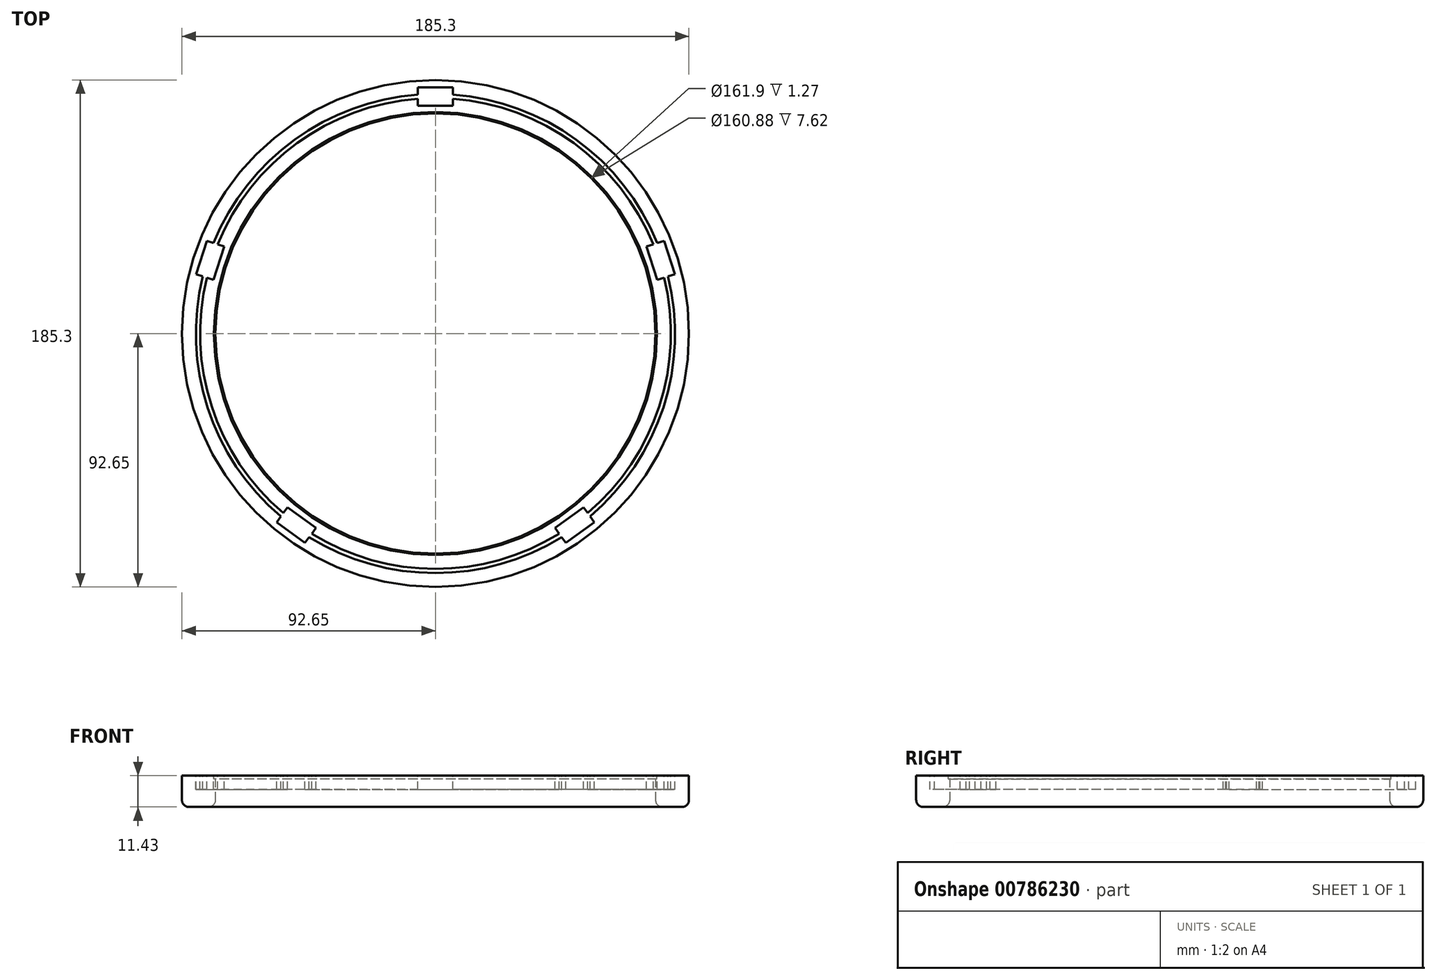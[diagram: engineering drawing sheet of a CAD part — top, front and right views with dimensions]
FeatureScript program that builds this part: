
annotation { "Feature Type Name" : "Feature", "Feature Type Description" : "" }
export const myFeature = defineFeature(function(context is Context, id is Id, definition is map)
    precondition{}
    {
        {
            var Q0;
            Q0=qCreatedBy(makeId("Front.planeOp"),FACE);
            var sketch = newSketch(context, id + "F0", { "sketchPlane" : qUnion([Q0])});
            skLineSegment(sketch, "E0", {"start": v(0, 91.39) * mm, "end": v(0, -94.44) * mm, "construction": true});
            skLineSegment(sketch, "E1", {"start": v(5.08, 0) * mm, "end": v(5.08, -10.16) * mm});
            skLineSegment(sketch, "E2", {"start": v(5.08, -10.16) * mm, "end": v(92.65, -10.16) * mm});
            skLineSegment(sketch, "E3", {"start": v(5.08, 0) * mm, "end": v(80.95, 0) * mm});
            skLineSegment(sketch, "E4.top", {"start": v(86.03, 1.27) * mm, "end": v(80.95, 1.27) * mm});
            skLineSegment(sketch, "E4.left", {"start": v(86.03, -3.8) * mm, "end": v(86.03, 1.27) * mm});
            skLineSegment(sketch, "E4.right", {"start": v(80.95, 0) * mm, "end": v(80.95, 1.27) * mm});
            skLineSegment(sketch, "E5.top", {"start": v(87.57, 1.27) * mm, "end": v(92.65, 1.27) * mm});
            skLineSegment(sketch, "E5.left", {"start": v(87.57, -3.8) * mm, "end": v(87.57, 1.27) * mm});
            skLineSegment(sketch, "E5.right", {"start": v(92.65, -10.16) * mm, "end": v(92.65, 1.27) * mm});
            skLineSegment(sketch, "E6", {"start": v(86.03, -3.8) * mm, "end": v(87.57, -3.8) * mm});
            skSolve(sketch);
        }
        {
            var Q0;
            Q0=qSketchRegion(id+"F0",true);
            var Q1;
            Q1=sQuery(id+"F0.wireOp",EDGE,"E0");
            revolve(context, id + "F1", {"surfaceOperationType" : NewSurfaceOperationType.NEW, "entities" : qUnion([Q0]), "axis" : qUnion([Q1]), "revolveType" : RevolveType.FULL});
        }
        {
            var Q0;
            Q0=makeQuery(id+"F1.opRevolve","SWEPT_FACE",FACE,{"disambiguationData":[OSD([sQuery(id+"F0.wireOp",EDGE,"E2")])]});
            var sketch = newSketch(context, id + "F2", { "sketchPlane" : qUnion([Q0])});
            skArc(sketch, "E7", {"start": v(-3.18, 80.38) * mm, "mid": v(-56.88, 56.88) * mm, "end": v(-80.38, 3.18) * mm});
            skLineSegment(sketch, "E8", {"start": v(0, 14.6) * mm, "end": v(0, 80.44) * mm, "construction": true});
            skLineSegment(sketch, "E9", {"start": v(14.6, 0) * mm, "end": v(80.44, 0) * mm, "construction": true});
            skLineSegment(sketch, "E10", {"start": v(0, -14.6) * mm, "end": v(0, -80.44) * mm, "construction": true});
            skLineSegment(sketch, "E11", {"start": v(-14.6, 0) * mm, "end": v(-80.44, 0) * mm, "construction": true});
            skArc(sketch, "E12.trimOffspring", {"start": v(-80.38, 3.18) * mm, "mid": v(-58, -55.75) * mm, "end": v(0, -80.44) * mm});
            skArc(sketch, "E13.trimOffspring", {"start": v(80.38, -3.17) * mm, "mid": v(56.88, 56.88) * mm, "end": v(-3.18, 80.38) * mm});
            skArc(sketch, "E14.trimOffspring", {"start": v(-3.17, -80.38) * mm, "mid": v(54.6, -59.08) * mm, "end": v(80.38, -3.17) * mm});
            skSolve(sketch);
        }
        {
            var Q0;
            Q0 = qSketchRegion(id + "F2", true);
            var Q1;
            Q1=makeQuery(id+"F1.opRevolve","SWEPT_FACE",FACE,{"disambiguationData":[OSD([sQuery(id+"F0.wireOp",EDGE,"E3")])]});
            extrude(context, id + "F3", {"entities" : qUnion([Q0, Q1]), "operationType" : NewBodyOperationType.REMOVE, "oppositeDirection" : true, "depth" : 25.4 * mm, "offsetDistance" : 25.4 * mm});
        }
        {
            var Q0;
            Q0=makeQuery(id+"F3.boolean.opBoolean","COPY",EDGE,{"derivedFrom":makeQuery(id+"F3.opExtrude","CAP_EDGE",EDGE,{"disambiguationData":[OSD([sQuery(id+"F2.wireOp",EDGE,"E7")])],"isStart":true})});
            var Q1;
            Q1=makeQuery(id+"F1.opRevolve","SWEPT_FACE",FACE,{"disambiguationData":[OSD([sQuery(id+"F0.wireOp",EDGE,"E2")])]});
            fillet(context, id + "F4", {"entities" : qUnion([Q0, Q1]), "radius" : 2.54 * mm, "tangentPropagation" : true, "allowEdgeOverflow" : false});
        }
        {
            var Q0;
            Q0=makeQuery(id+"F1.opRevolve","SWEPT_FACE",FACE,{"disambiguationData":[OSD([sQuery(id+"F0.wireOp",EDGE,"E5.top")])]});
            var sketch = newSketch(context, id + "F5", { "sketchPlane" : qUnion([Q0])});
            skLineSegment(sketch, "E15.bottom", {"start": v(-6.41, 89.93) * mm, "end": v(6.41, 89.93) * mm});
            skLineSegment(sketch, "E15.top", {"start": v(-6.41, 83.2) * mm, "end": v(6.41, 83.2) * mm});
            skLineSegment(sketch, "E15.left", {"start": v(-6.41, 89.93) * mm, "end": v(-6.41, 83.2) * mm});
            skLineSegment(sketch, "E15.right", {"start": v(6.41, 89.93) * mm, "end": v(6.41, 83.2) * mm});
            skPoint(sketch, "E16.center", {"position": v(0, 0) * mm});
            skLineSegment(sketch, "E17.1.0", {"start": v(-87.5, 21.69) * mm, "end": v(-83.55, 33.89) * mm});
            skLineSegment(sketch, "E17.1.1", {"start": v(-81.1, 19.6) * mm, "end": v(-77.14, 31.8) * mm});
            skLineSegment(sketch, "E17.1.2", {"start": v(-87.5, 21.69) * mm, "end": v(-81.1, 19.6) * mm});
            skLineSegment(sketch, "E17.1.3", {"start": v(-83.55, 33.89) * mm, "end": v(-77.14, 31.8) * mm});
            skLineSegment(sketch, "E17.2.0", {"start": v(-47.67, -76.52) * mm, "end": v(-58.05, -68.98) * mm});
            skLineSegment(sketch, "E17.2.1", {"start": v(-43.71, -71.08) * mm, "end": v(-54.1, -63.54) * mm});
            skLineSegment(sketch, "E17.2.2", {"start": v(-47.67, -76.52) * mm, "end": v(-43.71, -71.08) * mm});
            skLineSegment(sketch, "E17.2.3", {"start": v(-58.05, -68.98) * mm, "end": v(-54.1, -63.54) * mm});
            skLineSegment(sketch, "E17.3.0", {"start": v(58.05, -68.98) * mm, "end": v(47.67, -76.52) * mm});
            skLineSegment(sketch, "E17.3.1", {"start": v(54.1, -63.54) * mm, "end": v(43.71, -71.08) * mm});
            skLineSegment(sketch, "E17.3.2", {"start": v(58.05, -68.98) * mm, "end": v(54.1, -63.54) * mm});
            skLineSegment(sketch, "E17.3.3", {"start": v(47.67, -76.52) * mm, "end": v(43.71, -71.08) * mm});
            skLineSegment(sketch, "E17.4.0", {"start": v(83.55, 33.89) * mm, "end": v(87.5, 21.69) * mm});
            skLineSegment(sketch, "E17.4.1", {"start": v(77.14, 31.8) * mm, "end": v(81.1, 19.6) * mm});
            skLineSegment(sketch, "E17.4.2", {"start": v(83.55, 33.89) * mm, "end": v(77.14, 31.8) * mm});
            skLineSegment(sketch, "E17.4.3", {"start": v(87.5, 21.69) * mm, "end": v(81.1, 19.6) * mm});
            skSolve(sketch);
        }
        {
            var Q0;
            Q0 = qSketchRegion(id + "F5", true);
            extrude(context, id + "F6", {"entities" : qUnion([Q0]), "operationType" : NewBodyOperationType.REMOVE, "oppositeDirection" : true, "depth" : 5.08 * mm, "offsetDistance" : 25.4 * mm});
        }
        {
            var Q0;
            Q0=makeQuery(id+"F1.opRevolve","SWEPT_BODY",BODY,{"disambiguationData":[OSD([sQuery(id+"F0.wireOp",EDGE,"E1"),sQuery(id+"F0.wireOp",EDGE,"E2"),sQuery(id+"F0.wireOp",EDGE,"E3"),sQuery(id+"F0.wireOp",EDGE,"E4.top"),sQuery(id+"F0.wireOp",EDGE,"E4.left"),sQuery(id+"F0.wireOp",EDGE,"E4.right"),sQuery(id+"F0.wireOp",EDGE,"E5.top"),sQuery(id+"F0.wireOp",EDGE,"E5.left"),sQuery(id+"F0.wireOp",EDGE,"E5.right"),sQuery(id+"F0.wireOp",EDGE,"E6")])]});
            transform(context, id + "F7", {"entities" : qUnion([Q0]), "transformType" : TransformType.TRANSLATION_3D, "dx" : 0 * mm, "dy" : 0 * mm, "dz" : 0 * mm, "makeCopy" : true});
        }
        {
            var Q0;
            Q0=makeQuery(id+"F7.opPattern","COPY",BODY,{"derivedFrom":makeQuery(id+"F1.opRevolve","SWEPT_BODY",BODY,{"disambiguationData":[OSD([sQuery(id+"F0.wireOp",EDGE,"E1"),sQuery(id+"F0.wireOp",EDGE,"E2"),sQuery(id+"F0.wireOp",EDGE,"E3"),sQuery(id+"F0.wireOp",EDGE,"E4.top"),sQuery(id+"F0.wireOp",EDGE,"E4.left"),sQuery(id+"F0.wireOp",EDGE,"E4.right"),sQuery(id+"F0.wireOp",EDGE,"E5.top"),sQuery(id+"F0.wireOp",EDGE,"E5.left"),sQuery(id+"F0.wireOp",EDGE,"E5.right"),sQuery(id+"F0.wireOp",EDGE,"E6")])]}),"instanceName":"1"});
            deleteBodies(context, id + "F8", {"entities" : qUnion([Q0])});
        }
    });
